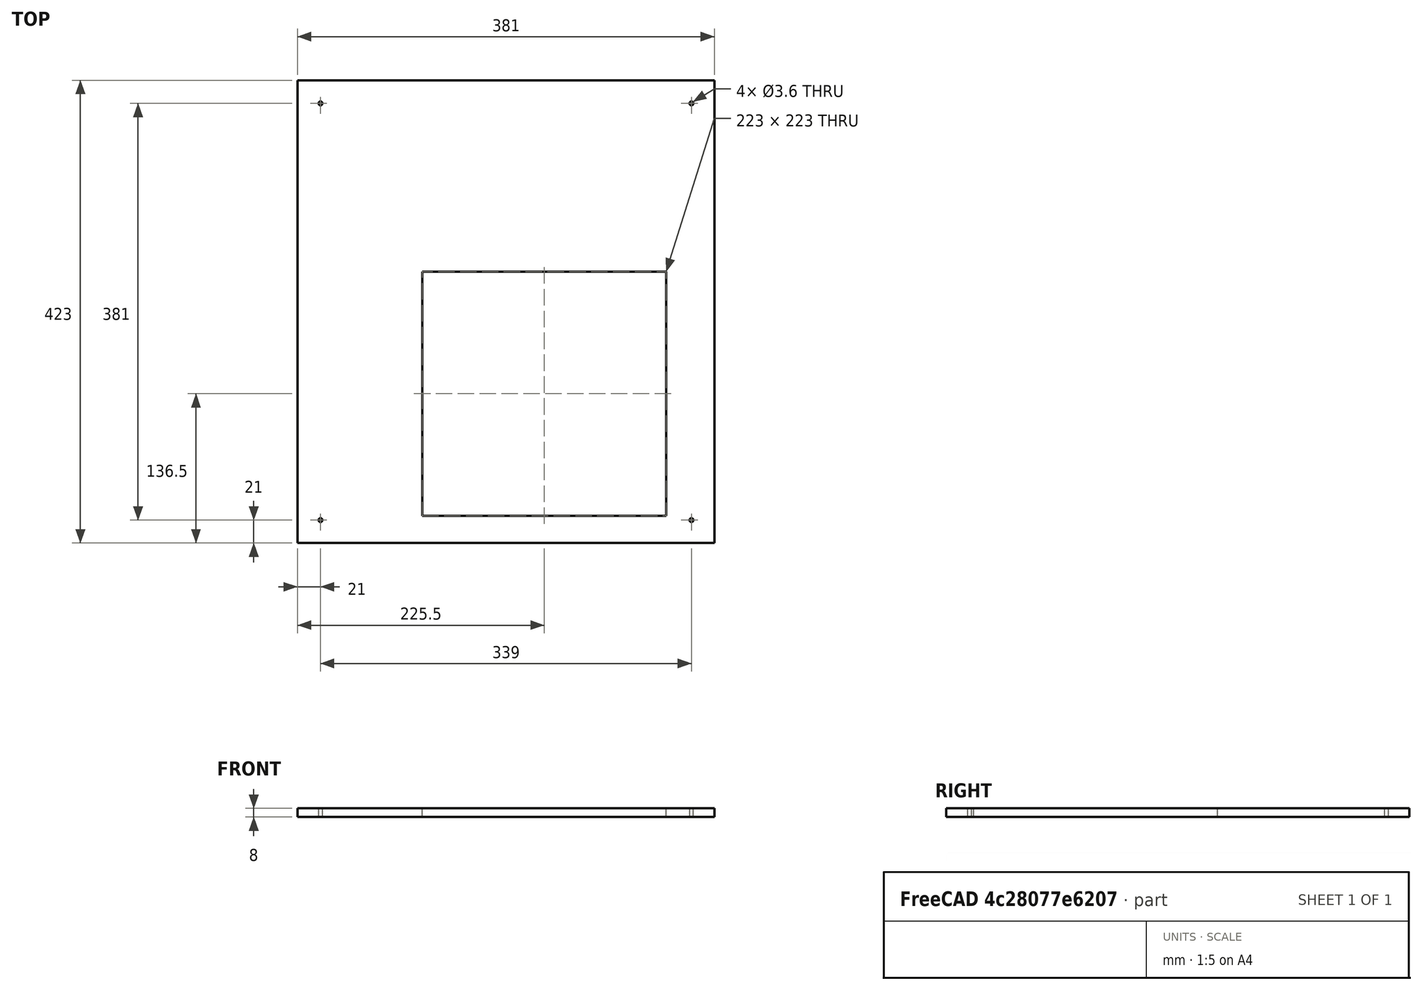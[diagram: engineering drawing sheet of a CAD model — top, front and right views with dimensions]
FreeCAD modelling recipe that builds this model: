
FCSTD DOCUMENT  (FreeCAD 0.16R6706 (Git))
Label: Teto
License: All rights reserved
LicenseURL: http://en.wikipedia.org/wiki/All_rights_reserved
objects: Sketcher::SketchObject×1, PartDesign::Pad×1
note: 3 computed .brp shape members not serialized (recipe doc carries the construction recipe); baked Part::Feature solids carry a one-line shape summary decoded from their .brp

FEATURE [Sketcher::SketchObject] Sketch
  sketch-geometry (16):
    g0: LineSegment StartX=-381 StartY=423 StartZ=0 EndX=0 EndY=423 EndZ=0
    g1: LineSegment StartX=0 StartY=423 StartZ=0 EndX=0 EndY=0 EndZ=0
    g2: LineSegment StartX=0 StartY=0 StartZ=0 EndX=-381 EndY=0 EndZ=0
    g3: LineSegment StartX=-381 StartY=0 StartZ=0 EndX=-381 EndY=423 EndZ=0
    g4: LineSegment StartX=-267 StartY=248 StartZ=0 EndX=-44 EndY=248 EndZ=0
    g5: LineSegment StartX=-44 StartY=248 StartZ=0 EndX=-44 EndY=25 EndZ=0
    g6: LineSegment StartX=-44 StartY=25 StartZ=0 EndX=-267 EndY=25 EndZ=0
    g7: LineSegment StartX=-267 StartY=25 StartZ=0 EndX=-267 EndY=248 EndZ=0
    g8: Circle CenterX=-360 CenterY=402 CenterZ=0 NormalX=0 NormalY=0 NormalZ=1 Radius=1.8
    g9: Circle CenterX=-21 CenterY=402 CenterZ=0 NormalX=0 NormalY=0 NormalZ=1 Radius=1.8
    g10: LineSegment [constr] StartX=-360 StartY=402 StartZ=0 EndX=-21 EndY=402 EndZ=0
    g11: LineSegment [constr] StartX=-21 StartY=402 StartZ=0 EndX=-21 EndY=21 EndZ=0
    g12: LineSegment [constr] StartX=-21 StartY=21 StartZ=0 EndX=-360 EndY=21 EndZ=0
    g13: LineSegment [constr] StartX=-360 StartY=21 StartZ=0 EndX=-360 EndY=402 EndZ=0
    g14: Circle CenterX=-360 CenterY=21 CenterZ=0 NormalX=0 NormalY=0 NormalZ=1 Radius=1.8
    g15: Circle CenterX=-21 CenterY=21 CenterZ=0 NormalX=0 NormalY=0 NormalZ=1 Radius=1.8
  constraints (42):
    c: Coincident(g0,g1)
    c: Coincident(g1,g2)
    c: Coincident(g2,g3)
    c: Coincident(g3,g0)
    c: Horizontal(g0)
    c: Horizontal(g2)
    c: Vertical(g1)
    c: Vertical(g3)
    c: DistanceX(g0,g0) = 381
    c: DistanceY(g1,g1) = 423
    c: Coincident(g-1,g1)
    c: Coincident(g4,g5)
    c: Coincident(g5,g6)
    c: Coincident(g6,g7)
    c: Coincident(g7,g4)
    c: Horizontal(g4)
    c: Horizontal(g6)
    c: Vertical(g5)
    c: Vertical(g7)
    c: DistanceX(g0,g4) = 114
    c: Radius(g8) = 1.8
    c: DistanceY(g9,g0) = 21
    c: Coincident(g10,g11)
    c: Coincident(g11,g12)
    c: Coincident(g12,g13)
    c: Coincident(g13,g10)
    c: Horizontal(g10)
    c: Horizontal(g12)
    c: Vertical(g11)
    c: Vertical(g13)
    c: DistanceY(g-1,g11) = 21
    c: DistanceX(g11,g-1) = 21
    c: DistanceX(g0,g10) = 21
    c: Equal(g8,g14) = 1.8
    c: Equal(g8,g15) = 1.8
    c: Coincident(g8,g10)
    c: Coincident(g9,g10)
    c: Coincident(g11,g15)
    c: Coincident(g12,g14)
    c: DistanceY(g2,g6) = 25
    c: DistanceY(g7,g7) = 223
    c: Equal(g7,g4)
FEATURE [PartDesign::Pad] Pad
  Length = 8
  Length2 = 100
  Sketch = -> Sketch
  Type = 0
